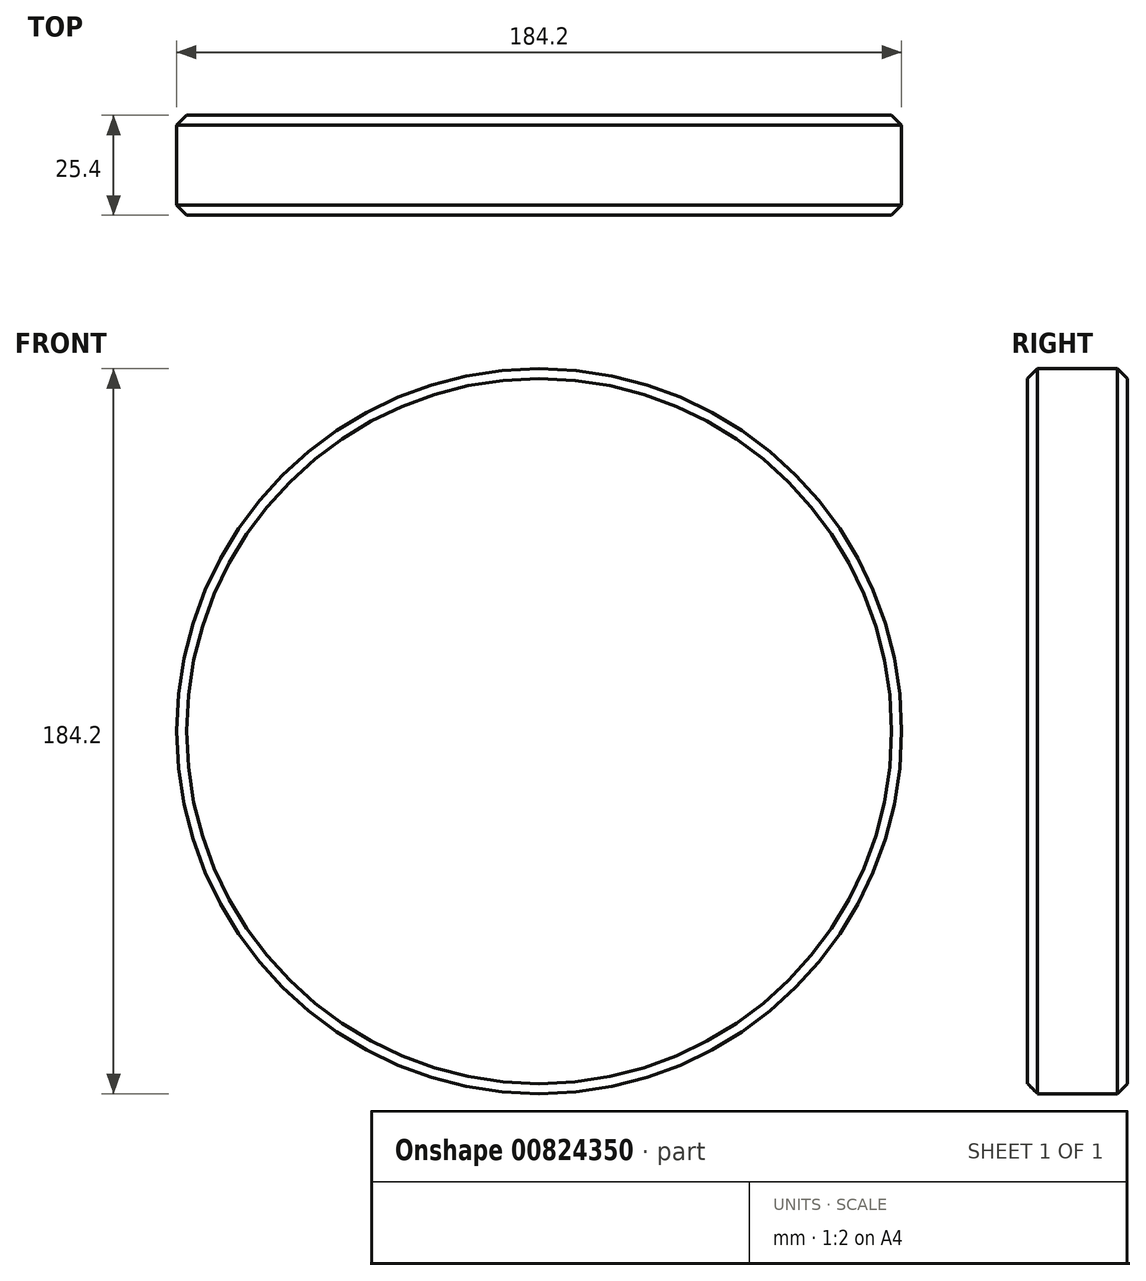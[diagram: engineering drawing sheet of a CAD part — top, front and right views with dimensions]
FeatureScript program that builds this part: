
annotation { "Feature Type Name" : "Feature", "Feature Type Description" : "" }
export const myFeature = defineFeature(function(context is Context, id is Id, definition is map)
    precondition{}
    {
        {
            var Q0;
            Q0=qCreatedBy(makeId("Front.planeOp"),FACE);
            var sketch = newSketch(context, id + "F0", { "sketchPlane" : qUnion([Q0])});
            skCircle(sketch, "E0", {"center": v(0, -92.1) * mm, "radius": 92.1 * mm});
            skSolve(sketch);
        }
        {
            var Q0;
            Q0 = qSketchRegion(id + "F0", true);
            extrude(context, id + "F1", {"entities" : qUnion([Q0]), "depth" : 25.4 * mm, "offsetDistance" : 25.4 * mm});
        }
        {
            var Q0;
            Q0=makeQuery(id+"F1.opExtrude","CAP_FACE",FACE,{"disambiguationData":[OSD([sQuery(id+"F0.wireOp",EDGE,"E0")])],"isStart":true});
            var Q1;
            Q1=makeQuery(id+"F1.opExtrude","CAP_EDGE",EDGE,{"disambiguationData":[OSD([sQuery(id+"F0.wireOp",EDGE,"E0")])],"isStart":false});
            chamfer(context, id + "F2", {"entities" : qUnion([Q0, Q1]), "width" : 2.54 * mm, "tangentPropagation" : true});
        }
    });
